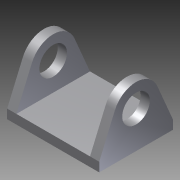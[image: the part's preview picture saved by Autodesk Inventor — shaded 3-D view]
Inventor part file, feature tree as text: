
AUTODESK INVENTOR PART (.ipt)
format: ipt  version: 2012 (Build 160160000, 160)  size: 114,176 bytes
history: native  units: in
note: dims shown in document units (in); Inventor stores cm internally (conversion verified against a paired STEP export)
features: extrude x2, sketch x2
ambient origin geometry x8: Origin, YZ Plane, XZ Plane, XY Plane, X Axis, Y Axis, Z Axis, Center Point
bodies: Solid1 (feature_tree)
feature tree (4):
  extrude  "Extrusion1"  Depth=1.25in
  extrude  "Extrusion2"  Depth=0.125in
  sketch  "Sketch1"  dims[d0=1.0in d1=1.25in]
  sketch  "Sketch2"  dims[d2=0.125in d3=0.125in d4=0.125in d5=1.0in d6=0.0in d9=0.375in d11=1.0in d12=0.0in d13=0.125in d14=0.5in d15=0.3125in d16=0.5in]
